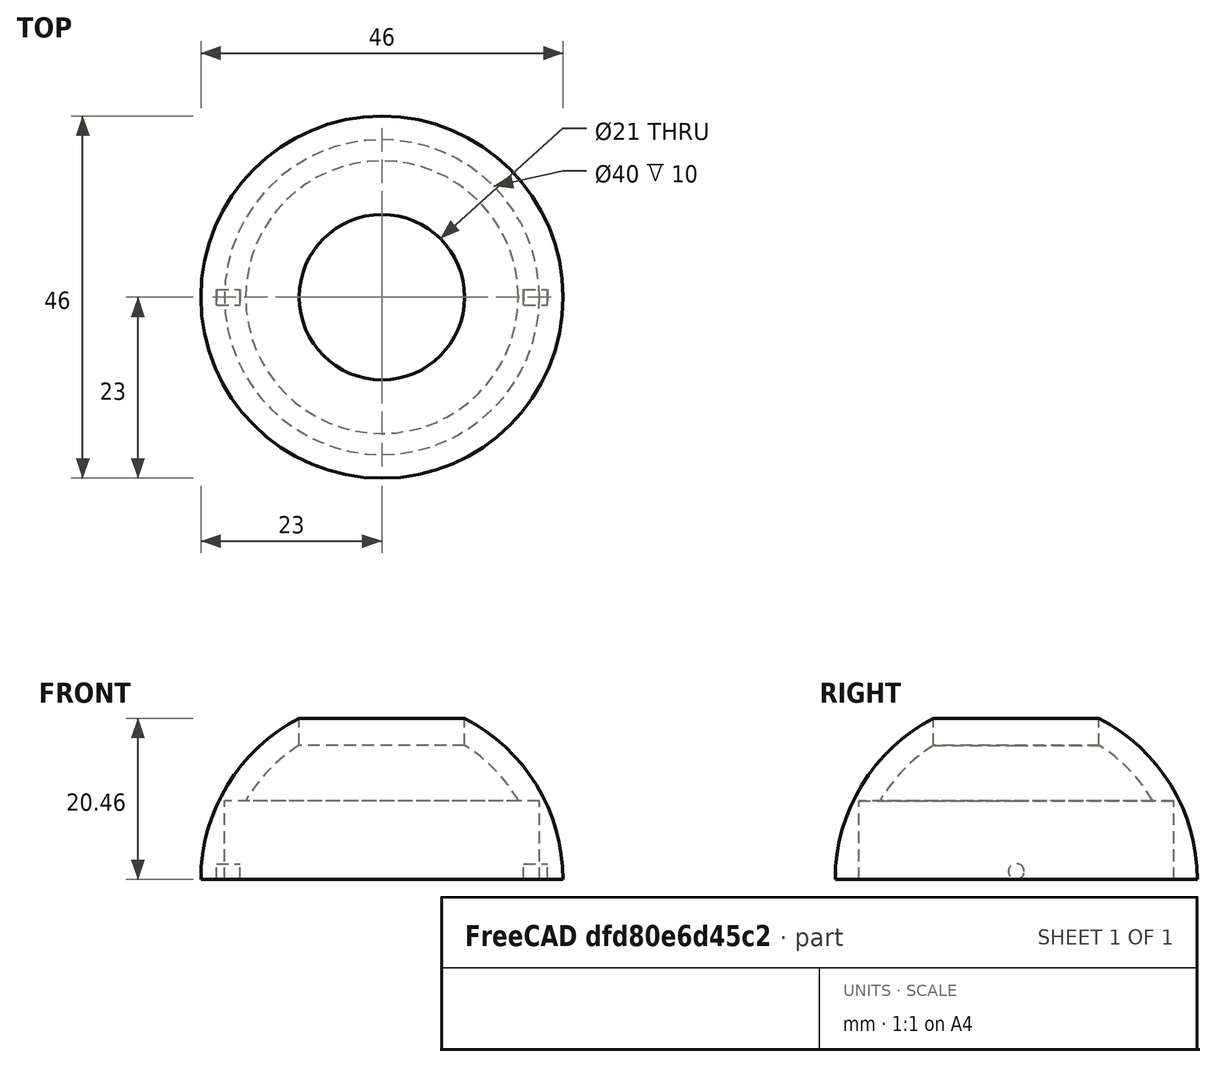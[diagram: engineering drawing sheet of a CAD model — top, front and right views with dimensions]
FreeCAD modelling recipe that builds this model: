
FCSTD DOCUMENT  (FreeCAD 0.18.4R)
Label: Top
License: All rights reserved
LicenseURL: http://en.wikipedia.org/wiki/All_rights_reserved
objects: Part::Cylinder×4, Part::Cut×3, Part::Sphere×2
note: 9 computed .brp shape members not serialized (recipe doc carries the construction recipe); baked Part::Feature solids carry a one-line shape summary decoded from their .brp

FEATURE [Part::Sphere] Sphere  label="Exterior"
  Angle1 = 0
  Angle2 = 90
  Angle3 = 360
  AttacherType = Attacher::AttachEngine3D
  Radius = 23
FEATURE [Part::Sphere] Sphere001  label="Interior"
  Angle1 = 0
  Angle2 = 90
  Angle3 = 360
  AttacherType = Attacher::AttachEngine3D
  Radius = 20
FEATURE [Part::Cut] Cut
  Base = -> Sphere
  Tool = -> Sphere001
FEATURE [Part::Cylinder] Cylinder  label="Button_pocket"
  Angle = 360
  AttacherType = Attacher::AttachEngine3D
  Height = 24
  Radius = 10.5
FEATURE [Part::Cut] Cut001
  Base = -> Cut
  Tool = -> Cylinder
FEATURE [Part::Cylinder] Cylinder001  label="Inner_space"
  Angle = 360
  AttacherType = Attacher::AttachEngine3D
  Height = 10
  Radius = 20.3
FEATURE [Part::Cut] Cut002
  Base = -> Cut001
  Tool = -> Cylinder001
FEATURE [Part::Cylinder] Cylinder002  label="Cilindro002"
  Angle = 360
  AttacherType = Attacher::AttachEngine3D
  Height = 3
  Placement = pos=(-21,0,1) rot=(0,1,0;1.5708rad)
  Radius = 1
FEATURE [Part::Cylinder] Cylinder003  label="Cilindro003"
  Angle = 360
  AttacherType = Attacher::AttachEngine3D
  Height = 3
  Placement = pos=(18,0,1) rot=(0,1,0;1.5708rad)
  Radius = 1
